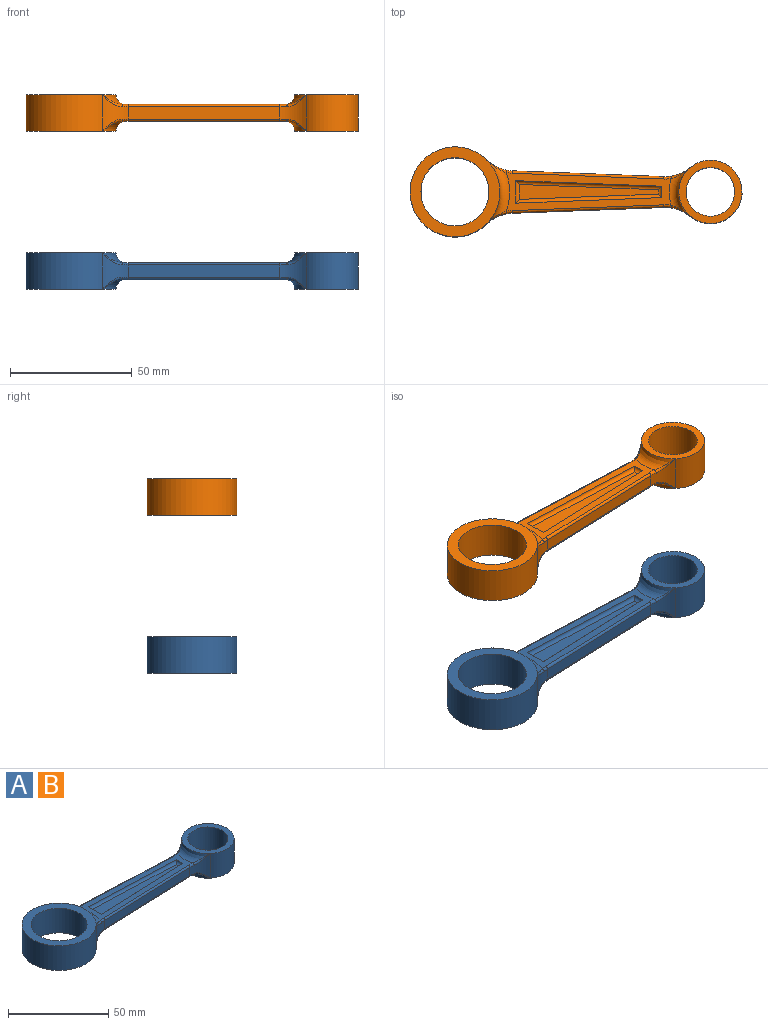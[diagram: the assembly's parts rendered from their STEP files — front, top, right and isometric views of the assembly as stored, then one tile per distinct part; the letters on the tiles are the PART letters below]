
ASSEMBLY  parts=2 mates=1
PART A: 50 faces, bbox 136.5x39.2x20.7 mm
  f0: plane 57x6.12mm, normal (0,0,-1), area 225.4mm2, adj f4,f5,f6,f7
  f1: plane 37x37mm, normal (0,0,-1), area 459.5mm2, adj f3,f10,f12
  f2: bspline ~9.36x5.53mm, area 8.8mm2, adj f9,f10,f15
  f3: cylinder r=14mm len=28mm, axis (0,0,1), area 1319.5mm2, adj f1,f16
  f4: cylinder r=1.5mm len=60.06mm, axis (1,0.04,0), area 138.9mm2, adj f0,f5,f7,f24
  f5: cylinder r=1.5mm len=9.23mm, axis (0,-1,0), area 19.1mm2, adj f0,f4,f6,f24
  f6: cylinder r=1.5mm len=60.06mm, axis (-1,0.04,0), area 138.9mm2, adj f0,f5,f7,f24
  f7: cylinder r=1.5mm len=4.68mm, axis (0,1,0), area 8.5mm2, adj f0,f4,f6,f24
  f8: cylinder r=1mm len=62.31mm, axis (-1,0.04,0), area 97.9mm2, adj f9,f20,f21,f24
  f9: torus R=17mm, axis (0,0,-1), area 3.7mm2, adj f2,f8,f15,f24
  f10: torus R=22.5mm, axis (0,0,-1), area 134.6mm2, adj f1,f2,f11,f24
  f11: bspline ~9.37x5.51mm, area 8.8mm2, adj f10,f13,f25
  f12: cylinder r=18.5mm len=37mm, axis (0,0,1), area 1301.5mm2, adj f1,f15,f16,f25
  f13: torus R=17mm, axis (0,0,-1), area 3.7mm2, adj f11,f24,f25,f26
  f14: plane 57x6.12mm, normal (0,0,1), area 225.4mm2, adj f27,f28,f29,f30
  f15: cylinder r=16mm len=15mm, axis (0,0,-1), area 94.1mm2, adj f2,f9,f12,f17,f20,f33
  f16: plane 37x37mm, normal (0,0,1), area 459.5mm2, adj f3,f12,f34
  f17: bspline ~9.36x5.53mm, area 8.8mm2, adj f15,f33,f34
  f18: bspline ~9.37x5.51mm, area 8.8mm2, adj f25,f31,f34
  f19: bspline ~8.95x5mm, area 8.5mm2, adj f21,f23,f36
  f20: plane 62.27x5mm, normal (0.04,1,0), area 311.6mm2, adj f8,f15,f32,f36
  f21: torus R=17mm, axis (0,0,-1), area 4.7mm2, adj f8,f19,f24,f36
  f22: plane 26x26mm, normal (0,0,-1), area 216.8mm2, adj f23,f37,f38
  f23: torus R=17mm, axis (0,0,-1), area 98mm2, adj f19,f22,f24,f39
  f24: plane 67.87x15.89mm, normal (0,0,-1), area 440.9mm2, adj f4,f5,f6,f7,f8,f9,f10,f13
  f25: cylinder r=16mm len=15mm, axis (0,0,1), area 93.9mm2, adj f11,f12,f13,f18,f31,f41
  f26: cylinder r=1mm len=62.44mm, axis (1,0.04,0), area 98.1mm2, adj f13,f24,f40,f41
  f27: cylinder r=1.5mm len=4.68mm, axis (0,1,0), area 8.5mm2, adj f14,f28,f30,f43
  f28: cylinder r=1.5mm len=60.06mm, axis (1,0.04,0), area 138.9mm2, adj f14,f27,f29,f43
  f29: cylinder r=1.5mm len=9.23mm, axis (0,-1,0), area 19.1mm2, adj f14,f28,f30,f43
  f30: cylinder r=1.5mm len=60.06mm, axis (-1,0.04,0), area 138.9mm2, adj f14,f27,f29,f43
  f31: torus R=17mm, axis (0,0,1), area 3.7mm2, adj f18,f25,f42,f43
  f32: cylinder r=1mm len=62.31mm, axis (1,-0.04,0), area 97.9mm2, adj f20,f33,f35,f43
  f33: torus R=17mm, axis (0,0,1), area 3.7mm2, adj f15,f17,f32,f43
  f34: torus R=22.5mm, axis (0,0,1), area 134.6mm2, adj f16,f17,f18,f43
  f35: torus R=17mm, axis (0,0,1), area 4.7mm2, adj f32,f36,f43,f44
  f36: cylinder r=16mm len=15mm, axis (0,0,1), area 90.7mm2, adj f19,f20,f21,f35,f38,f44
  f37: cylinder r=10mm len=20mm, axis (0,0,1), area 942.5mm2, adj f22,f45
  f38: cylinder r=13mm len=26mm, axis (0,0,1), area 883.1mm2, adj f22,f36,f45,f46
  f39: bspline ~8.96x5mm, area 8.5mm2, adj f23,f40,f46
  f40: torus R=17mm, axis (0,0,-1), area 4.7mm2, adj f24,f26,f39,f46
  f41: plane 62.4x5mm, normal (0.04,-1,0), area 312.2mm2, adj f25,f26,f42,f46
  f42: cylinder r=1mm len=62.44mm, axis (-1,-0.04,0), area 98.1mm2, adj f31,f41,f43,f47
  f43: plane 67.87x15.89mm, normal (0,0,1), area 440.9mm2, adj f27,f28,f29,f30,f31,f32,f33,f34
  f44: bspline ~8.95x5mm, area 8.5mm2, adj f35,f36,f48
  f45: plane 26x26mm, normal (0,0,1), area 216.8mm2, adj f37,f38,f48
  f46: cylinder r=16mm len=15mm, axis (0,0,-1), area 90.5mm2, adj f38,f39,f40,f41,f47,f49
  f47: torus R=17mm, axis (0,0,1), area 4.7mm2, adj f42,f43,f46,f49
  f48: torus R=17mm, axis (0,0,1), area 98mm2, adj f43,f44,f45,f49
  f49: bspline ~8.96x5mm, area 8.5mm2, adj f46,f47,f48
PART B: same geometry as A
PLACE A t=(30.39,-18.02,-46.7)mm
PLACE B t=(30.39,-18.02,18.3)mm
MATE cylindrical A.f3 <-> B.f3  axis (0,0,1) through (26.97,-17.85,-54.2)mm
